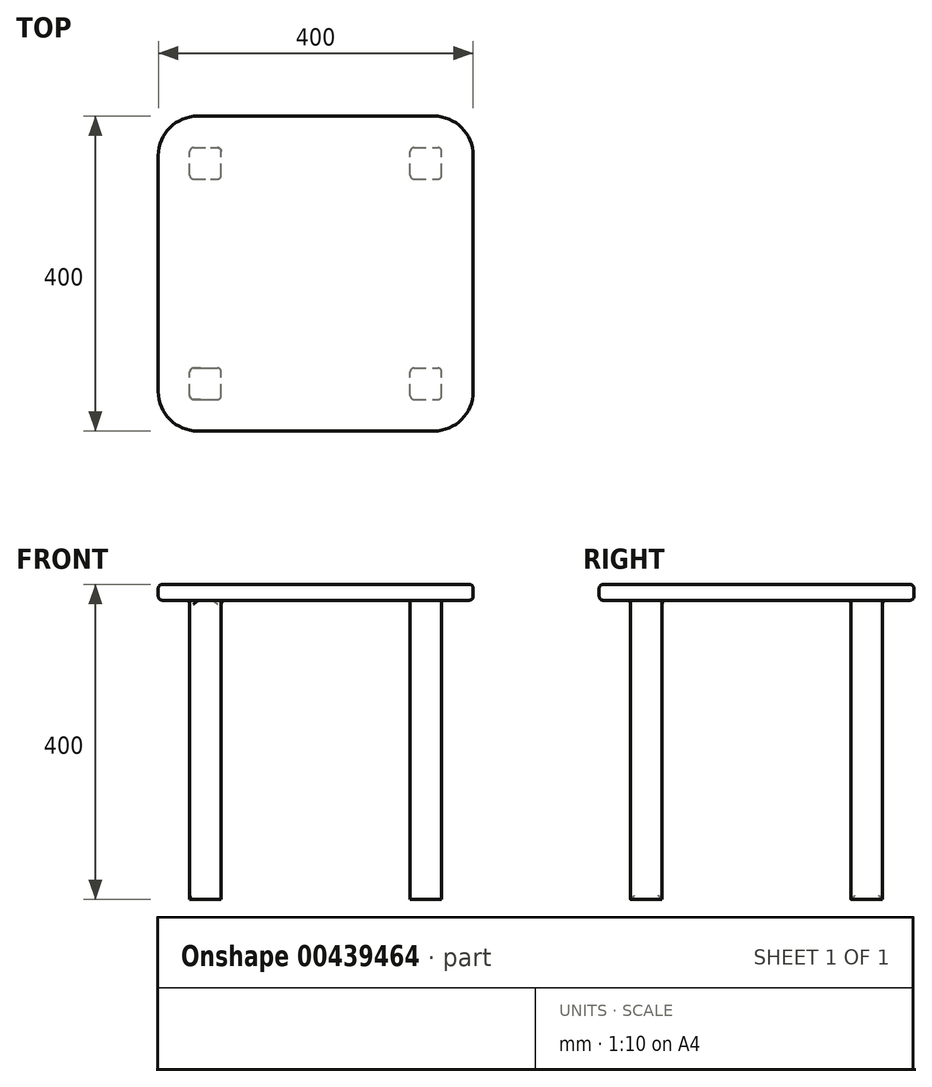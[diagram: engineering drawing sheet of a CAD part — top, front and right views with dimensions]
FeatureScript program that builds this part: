
annotation { "Feature Type Name" : "Feature", "Feature Type Description" : "" }
export const myFeature = defineFeature(function(context is Context, id is Id, definition is map)
    precondition{}
    {
        {
            var Q0;
            Q0=qCreatedBy(makeId("Top.planeOp"),FACE);
            var sketch = newSketch(context, id + "F0", { "sketchPlane" : qUnion([Q0])});
            skLineSegment(sketch, "E0.bottom", {"start": v(-194.07, 203.46) * mm, "end": v(105.93, 203.46) * mm});
            skLineSegment(sketch, "E0.top", {"start": v(-194.07, -196.54) * mm, "end": v(105.93, -196.54) * mm});
            skLineSegment(sketch, "E0.left", {"start": v(-244.07, 153.46) * mm, "end": v(-244.07, -146.54) * mm});
            skLineSegment(sketch, "E0.right", {"start": v(155.93, 153.46) * mm, "end": v(155.93, -146.54) * mm});
            skPoint(sketch, "E1.visualSharp", {"position": v(-244.07, 203.46) * mm});
            skArc(sketch, "E1.filletArc", {"start": v(-194.07, 203.46) * mm, "mid": v(-229.43, 188.82) * mm, "end": v(-244.07, 153.46) * mm});
            skPoint(sketch, "E2.visualSharp", {"position": v(155.93, 203.46) * mm});
            skArc(sketch, "E2.filletArc", {"start": v(155.93, 153.46) * mm, "mid": v(141.28, 188.82) * mm, "end": v(105.93, 203.46) * mm});
            skPoint(sketch, "E3.visualSharp", {"position": v(155.93, -196.54) * mm});
            skArc(sketch, "E3.filletArc", {"start": v(105.93, -196.54) * mm, "mid": v(141.28, -181.9) * mm, "end": v(155.93, -146.54) * mm});
            skPoint(sketch, "E4.visualSharp", {"position": v(-244.07, -196.54) * mm});
            skArc(sketch, "E4.filletArc", {"start": v(-244.07, -146.54) * mm, "mid": v(-229.43, -181.9) * mm, "end": v(-194.07, -196.54) * mm});
            skSolve(sketch);
        }
        {
            var Q0;
            Q0=makeQuery(id+"F0.imprint","IMPRINT",FACE,{"disambiguationData":[TD([[makeQuery(id+"F0.imprint","IMPRINT",EDGE,{"derivedFrom":sQuery(id+"F0.wireOp",EDGE,"E0.bottom")}),-1.0]])]});
            extrude(context, id + "F1", {"entities" : qUnion([Q0]), "depth" : 20 * mm});
        }
        {
            var Q0;
            Q0=makeQuery(id+"F1.opExtrude","CAP_FACE",FACE,{"disambiguationData":[OSD([sQuery(id+"F0.wireOp",EDGE,"E0.bottom"),sQuery(id+"F0.wireOp",EDGE,"E0.top"),sQuery(id+"F0.wireOp",EDGE,"E0.left"),sQuery(id+"F0.wireOp",EDGE,"E0.right"),sQuery(id+"F0.wireOp",EDGE,"E1.filletArc"),sQuery(id+"F0.wireOp",EDGE,"E2.filletArc"),sQuery(id+"F0.wireOp",EDGE,"E3.filletArc"),sQuery(id+"F0.wireOp",EDGE,"E4.filletArc")])],"isStart":true});
            fillet(context, id + "F2", {"entities" : qUnion([Q0]), "radius" : 5 * mm, "tangentPropagation" : true, "allowEdgeOverflow" : false});
        }
        {
            var Q0;
            Q0=makeQuery(id+"F1.opExtrude","CAP_FACE",FACE,{"disambiguationData":[OSD([sQuery(id+"F0.wireOp",EDGE,"E0.bottom"),sQuery(id+"F0.wireOp",EDGE,"E0.top"),sQuery(id+"F0.wireOp",EDGE,"E0.left"),sQuery(id+"F0.wireOp",EDGE,"E0.right"),sQuery(id+"F0.wireOp",EDGE,"E1.filletArc"),sQuery(id+"F0.wireOp",EDGE,"E2.filletArc"),sQuery(id+"F0.wireOp",EDGE,"E3.filletArc"),sQuery(id+"F0.wireOp",EDGE,"E4.filletArc")])],"isStart":true});
            var sketch = newSketch(context, id + "F3", { "sketchPlane" : qUnion([Q0])});
            skLineSegment(sketch, "E5.bottom", {"start": v(-204.07, 156.54) * mm, "end": v(-164.07, 156.54) * mm});
            skLineSegment(sketch, "E5.top", {"start": v(-204.07, 116.54) * mm, "end": v(-164.07, 116.54) * mm});
            skLineSegment(sketch, "E5.left", {"start": v(-204.07, 156.54) * mm, "end": v(-204.07, 116.54) * mm});
            skLineSegment(sketch, "E5.right", {"start": v(-164.07, 156.54) * mm, "end": v(-164.07, 116.54) * mm});
            skLineSegment(sketch, "E6.bottom", {"start": v(75.93, 156.54) * mm, "end": v(115.93, 156.54) * mm});
            skLineSegment(sketch, "E6.top", {"start": v(75.93, 116.54) * mm, "end": v(115.93, 116.54) * mm});
            skLineSegment(sketch, "E6.left", {"start": v(75.93, 156.54) * mm, "end": v(75.93, 116.54) * mm});
            skLineSegment(sketch, "E6.right", {"start": v(115.93, 156.54) * mm, "end": v(115.93, 116.54) * mm});
            skLineSegment(sketch, "E7.bottom", {"start": v(-204.07, -123.46) * mm, "end": v(-164.07, -123.46) * mm});
            skLineSegment(sketch, "E7.top", {"start": v(-204.07, -163.46) * mm, "end": v(-164.07, -163.46) * mm});
            skLineSegment(sketch, "E7.left", {"start": v(-204.07, -123.46) * mm, "end": v(-204.07, -163.46) * mm});
            skLineSegment(sketch, "E7.right", {"start": v(-164.07, -123.46) * mm, "end": v(-164.07, -163.46) * mm});
            skLineSegment(sketch, "E8.bottom", {"start": v(75.93, -123.46) * mm, "end": v(115.93, -123.46) * mm});
            skLineSegment(sketch, "E8.top", {"start": v(75.93, -163.46) * mm, "end": v(115.93, -163.46) * mm});
            skLineSegment(sketch, "E8.left", {"start": v(75.93, -123.46) * mm, "end": v(75.93, -163.46) * mm});
            skLineSegment(sketch, "E8.right", {"start": v(115.93, -123.46) * mm, "end": v(115.93, -163.46) * mm});
            skSolve(sketch);
        }
        {
            var Q0;
            Q0=makeQuery(id+"F3.imprint","IMPRINT",FACE,{"disambiguationData":[TD([[makeQuery(id+"F3.imprint","IMPRINT",EDGE,{"derivedFrom":sQuery(id+"F3.wireOp",EDGE,"E6.bottom")}),-1.0]])]});
            var Q1;
            Q1=makeQuery(id+"F3.imprint","IMPRINT",FACE,{"disambiguationData":[TD([[makeQuery(id+"F3.imprint","IMPRINT",EDGE,{"derivedFrom":sQuery(id+"F3.wireOp",EDGE,"E8.bottom")}),-1.0]])]});
            var Q2;
            Q2=makeQuery(id+"F3.imprint","IMPRINT",FACE,{"disambiguationData":[TD([[makeQuery(id+"F3.imprint","IMPRINT",EDGE,{"derivedFrom":sQuery(id+"F3.wireOp",EDGE,"E7.bottom")}),-1.0]])]});
            var Q3;
            Q3=makeQuery(id+"F3.imprint","IMPRINT",FACE,{"disambiguationData":[TD([[makeQuery(id+"F3.imprint","IMPRINT",EDGE,{"derivedFrom":sQuery(id+"F3.wireOp",EDGE,"E5.bottom")}),-1.0]])]});
            extrude(context, id + "F4", {"entities" : qUnion([Q0, Q1, Q2, Q3]), "operationType" : NewBodyOperationType.ADD, "depth" : 380 * mm});
        }
        {
            var Q0;
            Q0=makeQuery(id+"F4.opExtrude","SWEPT_EDGE",EDGE,{"disambiguationData":[OSD([sQuery(id+"F3.wireOp",EDGE,"E5.bottom"),sQuery(id+"F3.wireOp",EDGE,"E5.right")])]});
            var Q1;
            Q1=makeQuery(id+"F4.opExtrude","SWEPT_EDGE",EDGE,{"disambiguationData":[OSD([sQuery(id+"F3.wireOp",EDGE,"E5.top"),sQuery(id+"F3.wireOp",EDGE,"E5.right")])]});
            var Q2;
            Q2=makeQuery(id+"F4.opExtrude","SWEPT_EDGE",EDGE,{"disambiguationData":[OSD([sQuery(id+"F3.wireOp",EDGE,"E5.bottom"),sQuery(id+"F3.wireOp",EDGE,"E5.left")])]});
            var Q3;
            Q3=makeQuery(id+"F4.opExtrude","SWEPT_FACE",FACE,{"disambiguationData":[OSD([sQuery(id+"F3.wireOp",EDGE,"E5.left")])]});
            var Q4;
            Q4=makeQuery(id+"F4.opExtrude","SWEPT_EDGE",EDGE,{"disambiguationData":[OSD([sQuery(id+"F3.wireOp",EDGE,"E6.bottom"),sQuery(id+"F3.wireOp",EDGE,"E6.left")])]});
            var Q5;
            Q5=makeQuery(id+"F4.opExtrude","SWEPT_EDGE",EDGE,{"disambiguationData":[OSD([sQuery(id+"F3.wireOp",EDGE,"E6.bottom"),sQuery(id+"F3.wireOp",EDGE,"E6.right")])]});
            var Q6;
            Q6=makeQuery(id+"F4.opExtrude","SWEPT_EDGE",EDGE,{"disambiguationData":[OSD([sQuery(id+"F3.wireOp",EDGE,"E6.top"),sQuery(id+"F3.wireOp",EDGE,"E6.right")])]});
            var Q7;
            Q7=makeQuery(id+"F4.opExtrude","SWEPT_EDGE",EDGE,{"disambiguationData":[OSD([sQuery(id+"F3.wireOp",EDGE,"E6.top"),sQuery(id+"F3.wireOp",EDGE,"E6.left")])]});
            var Q8;
            Q8=makeQuery(id+"F4.opExtrude","SWEPT_EDGE",EDGE,{"disambiguationData":[OSD([sQuery(id+"F3.wireOp",EDGE,"E8.bottom"),sQuery(id+"F3.wireOp",EDGE,"E8.right")])]});
            var Q9;
            Q9=makeQuery(id+"F4.opExtrude","SWEPT_EDGE",EDGE,{"disambiguationData":[OSD([sQuery(id+"F3.wireOp",EDGE,"E8.top"),sQuery(id+"F3.wireOp",EDGE,"E8.right")])]});
            var Q10;
            Q10=makeQuery(id+"F4.opExtrude","SWEPT_EDGE",EDGE,{"disambiguationData":[OSD([sQuery(id+"F3.wireOp",EDGE,"E8.top"),sQuery(id+"F3.wireOp",EDGE,"E8.left")])]});
            var Q11;
            Q11=makeQuery(id+"F4.opExtrude","SWEPT_EDGE",EDGE,{"disambiguationData":[OSD([sQuery(id+"F3.wireOp",EDGE,"E8.bottom"),sQuery(id+"F3.wireOp",EDGE,"E8.left")])]});
            var Q12;
            Q12=makeQuery(id+"F4.opExtrude","SWEPT_EDGE",EDGE,{"disambiguationData":[OSD([sQuery(id+"F3.wireOp",EDGE,"E7.top"),sQuery(id+"F3.wireOp",EDGE,"E7.left")])]});
            var Q13;
            Q13=makeQuery(id+"F4.opExtrude","SWEPT_EDGE",EDGE,{"disambiguationData":[OSD([sQuery(id+"F3.wireOp",EDGE,"E7.bottom"),sQuery(id+"F3.wireOp",EDGE,"E7.left")])]});
            var Q14;
            Q14=makeQuery(id+"F4.opExtrude","SWEPT_EDGE",EDGE,{"disambiguationData":[OSD([sQuery(id+"F3.wireOp",EDGE,"E7.top"),sQuery(id+"F3.wireOp",EDGE,"E7.right")])]});
            var Q15;
            Q15=makeQuery(id+"F4.opExtrude","SWEPT_FACE",FACE,{"disambiguationData":[OSD([sQuery(id+"F3.wireOp",EDGE,"E7.right")])]});
            fillet(context, id + "F5", {"entities" : qUnion([Q0, Q1, Q2, Q3, Q4, Q5, Q6, Q7, Q8, Q9, Q10, Q11, Q12, Q13, Q14, Q15]), "radius" : 5 * mm, "tangentPropagation" : true, "allowEdgeOverflow" : false});
        }
        {
            var Q0;
            Q0=makeQuery(id+"F1.opExtrude","CAP_FACE",FACE,{"disambiguationData":[OSD([sQuery(id+"F0.wireOp",EDGE,"E0.bottom"),sQuery(id+"F0.wireOp",EDGE,"E0.top"),sQuery(id+"F0.wireOp",EDGE,"E0.left"),sQuery(id+"F0.wireOp",EDGE,"E0.right"),sQuery(id+"F0.wireOp",EDGE,"E1.filletArc"),sQuery(id+"F0.wireOp",EDGE,"E2.filletArc"),sQuery(id+"F0.wireOp",EDGE,"E3.filletArc"),sQuery(id+"F0.wireOp",EDGE,"E4.filletArc")])],"isStart":false});
            fillet(context, id + "F6", {"entities" : qUnion([Q0]), "radius" : 5 * mm, "tangentPropagation" : true, "allowEdgeOverflow" : false});
        }
    });
